# Revit family: WashBasin-CounterTop-SoftSquareBowl-60cm-WithTapHole-Vitra-GeoSeries-7426
name_source: partatom
category: Plumbing Fixtures
revit_build: Autodesk Revit 2017 (Build: 20160225_1515(x64)
units: mm (PartAtom-declared; Revit-internal decimal feet)

## family parameters
Cut with Voids When Loaded = No
Host = Face
OmniClass Number = 23.45.05.14.14
OmniClass Title = Sinks/Lavatories
Part Type = Normal
Room Calculation Point = No
Round Connector Dimension = Use Diameter
Shared = Yes

## types (10) — shared parameters
BIMobject category = Sanitary - Basins
Brand = VitrA
CW Connection = No
Default Elevation = 800 mm  [stored 2.62467 ft]
Design country = Turkey
HW Connection = No
IFC Classification = Sanitary Terminal
Main Material = Ceramic
Masterformat 2014 Code = 22 41 16
Masterformat 2014 Description = Residential Lavatories and Sinks
Mounting type = Counter Top Washbasins
NBS Referans Code = 35-65-70-94
NBS Referans Description = Wash Basin Systems
Nominal Depth (mm) = 430 mm
Nominal Height (mm) = 150 mm
Nominal Width (mm) = 600 mm
OmniClass Code = 23.45.05.14.14
OmniClass Description = Sinks/Lavatories
Product certification = https://www.vitraglobal.com
Product family = Counter Top Washbasins
Product group = Geo
URL = https://vitraglobal.com
Uniclass 1.4 Code = L7212
Uniclass 1.4 Description = Washbasins
Uniclass 2.0 Code = SS-35-65-70-94
Uniclass 2.0 Description = Sanitary Dispensing And Disposal Units
Uniclass 2015 Code = Pr_40_20_96_81
Uniclass 2015 Name = Wash basins, Sinks and troughs
Uniformat II Code = D2010
Uniformat II Description = Plumbing Fixtures
Vent Connection = No
Warranty Period (Year) = 10 Years
Waste Connection = Yes
Youtube = https://www.youtube.com

## per-type parameters (varying)
| type | Article No. (default) | Color | Description | Manufacturer | Manufacturer name | Model | Primary Material | Product SKU | Product url | Technical description | Weight Net (kg) | Without Overflow Hole |
| WashBasin-CounterTop-SoftSquareBowl-60cm-WithTapHole-WithOverflowHole-Vitra-GeoSeries_7426B483H0001 | 7426B483H0001 | White | VitrA Geo, Soft-Square Bowl 60 cm, soft-square bowl, with tap hole, with overflow hole | Vitra | Vitra | 7426B483H0001 | Matte Black | 7426B483H0001 | https://www.vitra-india.com | https://www.vitra-india.com | 16.2 | No |
| WashBasin-CounterTop-SoftSquareBowl-60cm-WithTapHole-WithOverflowHole-Vitra-GeoSeries_7426B420H0001 | 7426B420H0001 | White | VitrA Geo, Soft-Square Bowl 60 cm, soft-square bowl, with tap hole, with overflow hole | Vitra | Vitra | 7426B420H0001 | Matte Taupe | 7426B420H0001 | https://www.vitra-india.com | https://www.vitra-india.com | 16.2 | No |
| WashBasin-CounterTop-SoftSquareBowl-60cm-WithTapHole-WithOverflowHole-Vitra-GeoSeries_7426B003H0001 | 7426B003H0001 | White | VitrA Geo, Soft-Square Bowl 60 cm, soft-square bowl, with tap hole, with overflow hole | Vitra | Vitra | 7426B003H0001 | White | 7426B003H0001 | https://www.vitra-india.com | https://www.vitra-india.com | 16.2 | No |
| WashBasin-CounterTop-SoftSquareBowl-60cm-WithTapHole-WithoutOverflowHole-Vitra-GeoSeries_7426B003-0041 | 7426B003-0041 | White | VitrA Geo, Soft-Square Bowl 60 cm, soft-square bowl, with tap hole, without overflow hole | Vitra | Vitra | 7426B003-0041 | White | 7426B003-0041 | https://www.vitra.co.uk | https://www.vitra.co.uk | 16.2 | Yes |
| WashBasin-CounterTop-SoftSquareBowl-60cm-WithTapHole-WithOverflowHole-Vitra-GeoSeries_7426B003-0001 | 7426B003-0001 | White | VitrA Geo - Soft-Square Bowl 60cm - soft-square bowl with tap hole - with overflow hole | Vitra | Vitra | 7426B003-0001 | White | 7426B003-0001 | https://www.vitra.co.uk | https://www.vitra.co.uk | 16.2 | No |
| WashBasin-CounterTop-SoftSquareBowl-60cm-WithTapHole-WithOverflowHole-Vitra-GeoSeries_7426B001-0001 | 7426B001-0001 | Matt White | VitrA Geo - Soft-Square Bowl 60cm - soft-square bowl with tap hole - with overflow hole | Vitra | Vitra | 7426B001-0001 | Matte White (Ceramic) | 7426B001-0001 | https://www.vitra.com.tr | https://www.vitra.com.tr | 16.2 | No |
| WashBasin-CounterTop-SoftSquareBowl-60cm-WithTapHole-WithOverflowHole-Vitra-GeoSeries_7426B020-0001 | 7426B020-0001 | Matt Beige | VitrA Geo - Soft-Square Bowl 60cm - soft-square bowl with tap hole - with overflow hole | Vitra | Vitra | 7426B020-0001 | Matte Beige (Ceramic) | 7426B020-0001 | https://www.vitra.com.tr | https://www.vitra.com.tr | 16.2 | No |
| WashBasin-CounterTop-SoftSquareBowl-60cm-WithTapHole-WithOverflowHole-Vitra-GeoSeries_7426B070-0001 | 7426B070-0001 | Black | VitrA Geo - Soft-Square Bowl 60cm - soft-square bowl with tap hole - with overflow hole | Vitra | Vitra | 7426B070-0001 | Black (Ceramic) | 7426B070-0001 | https://www.vitra.com.tr | https://www.vitra.com.tr | 16.2 | No |
| WashBasin-CounterTop-SoftSquareBowl-60cm-WithTapHole-WithOverflowHole-Vitra-GeoSeries_7426B083-0001 | 7426B083-0001 | Matt Black | VitrA Geo - Soft-Square Bowl 60cm - soft-square bowl with tap hole - with overflow hole | Vitra | Vitra | 7426B083-0001 | Matte Black (Ceramic) | 7426B083-0001 | https://www.vitra.com.tr | https://www.vitra.com.tr | 16.2 | No |
| WashBasin-CounterTop-SoftSquareBowl-60cm-WithTapHole-WithOverflowHole-Vitra-GeoSeries_7426B003-7200 | 7426B003-7200 | Matt Black | VitrA Geo - Soft-Square Bowl 60cm - soft-square bowl with tap hole - with overflow hole | VitrA | VitrA | 7426B003-7200 | Matte Black (Ceramic) | 7426B003-7200 | https://www.vitra.com.tr | https://www.vitra.com.tr | 16.4 | No |

note: [stored X ft] marks values corroborated as IEEE doubles in the binary element streams (Revit-internal decimal feet)

## geometry (parser evidence)
native form markers: Sweep x2
no freeform markers — native parametric forms only
